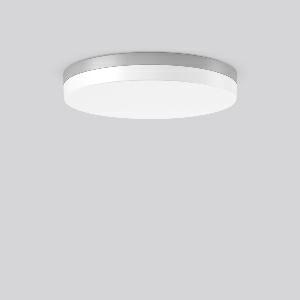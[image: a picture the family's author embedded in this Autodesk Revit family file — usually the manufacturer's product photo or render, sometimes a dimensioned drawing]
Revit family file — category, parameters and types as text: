
# Revit family: flat_slim_round_312678_004_19_81d6
name_source: partatom
category: Lighting Fixtures
units: mm (PartAtom-declared; Revit-internal decimal feet)

## family parameters
Cut with Voids When Loaded = No
Host = Face
Light Source = No
Part Type = Normal
Room Calculation Point = No
Round Connector Dimension = Use Diameter
Shared = No

## types (1)
- MultiLumen 1 830 (1 x LED Modul 830, 3450 lm, 3000)
    Apparent Load = 26 VA
    CIE Flux Codes = 40 71 90 84 100
    Color Rendering = 80
    Color Temperature = 3000
    Default Elevation = 1800 mm
    Height = 70 mm
    Lamp = 1 x LED Modul 830
    Lamp Light Flux = 3450 lm
    Lamp count = 1
    Length = 480 mm
    Lifetime = 50000 h
    Luminous efficacy = 133 lm/W
    Manufacturer = RZB
    ModVariant = No
    Model = 312678.004.19
    Mounting Place = Ceiling
    Mounting Type = Surface mounted
    Number of Poles = 1
    OnlyDefault = Yes
    Power Factor = 1
    Product Name = FLAT SLIM round
    Product group = Surface mounted ceiling and wall luminaires
    ProductGroupID = 305
    Protection Class = Protection class I
    Protection Degree = Degree of protection
    RLX_Detail_Level = 1
    RLX_Emergency_Light_Flux = 0 lm
    RLX_Emergency_Type = 0
    RLX_Emergency_Type_DB = No
    RlxData = <blob elided: 22513 chars, md5=07e51dac>
    Socket = socket
    Standby Power = 0 W
    System Light Flux = 3450 lm
    System Power = 26 W
    Type Comments = MultiLumen 1 830
    Type Image = 312633.004.jpg
    URL = http://relux.com
    VarID = multilumen_1_830
    Voltage = 0 V
    Weight = 0.00 kg
    Width = 0 mm  [stored 0 ft]

note: [stored X ft] marks values corroborated as IEEE doubles in the binary element streams (Revit-internal decimal feet)

## geometry (parser evidence)
native form markers: Blend x4, Sweep x11
no freeform markers — native parametric forms only
